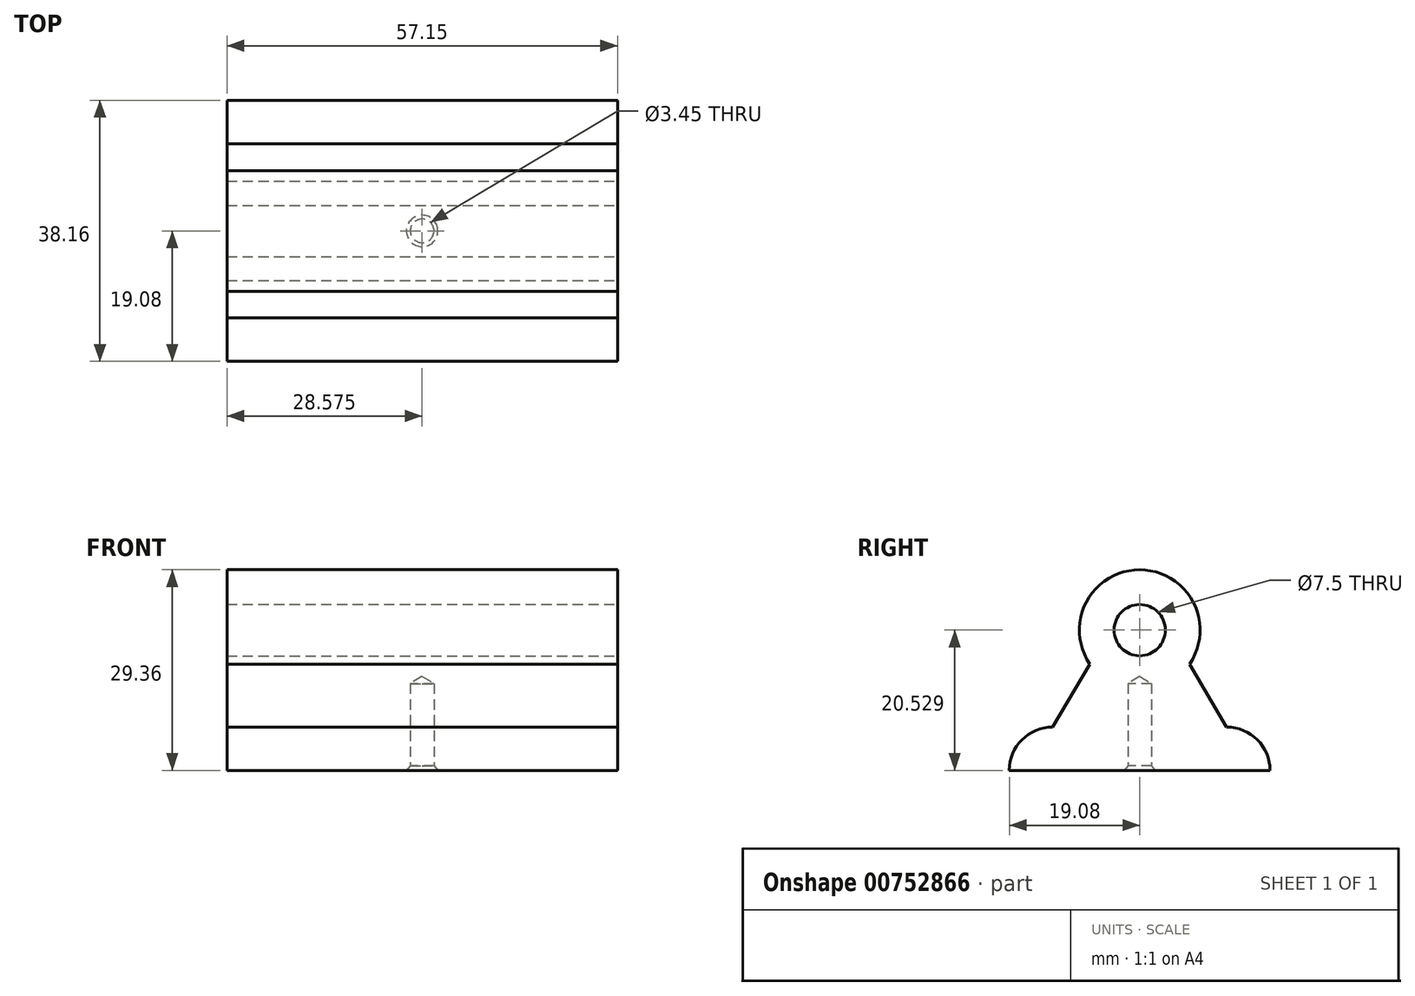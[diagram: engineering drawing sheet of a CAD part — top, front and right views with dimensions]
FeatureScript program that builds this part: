
annotation { "Feature Type Name" : "Feature", "Feature Type Description" : "" }
export const myFeature = defineFeature(function(context is Context, id is Id, definition is map)
    precondition{}
    {
        {
            var Q0;
            Q0=qCreatedBy(makeId("Right.planeOp"),FACE);
            var sketch = newSketch(context, id + "F0", { "sketchPlane" : qUnion([Q0])});
            skCircle(sketch, "E0", {"center": v(0, 2.7) * mm, "radius": 25 * mm});
            skCircle(sketch, "E1", {"center": v(0, 16.7) * mm, "radius": 11 * mm});
            skCircle(sketch, "E2", {"center": v(0, 16.7) * mm, "radius": 3.75 * mm});
            skLineSegment(sketch, "E3.bottom", {"start": v(12.73, 2.53) * mm, "end": v(-12.73, 2.53) * mm});
            skLineSegment(sketch, "E3.top", {"start": v(12.73, -10.17) * mm, "end": v(-12.73, -10.17) * mm});
            skLineSegment(sketch, "E3.left", {"start": v(19.08, -3.82) * mm, "end": v(19.08, -3.82) * mm});
            skLineSegment(sketch, "E3.right", {"start": v(-19.08, -3.82) * mm, "end": v(-19.08, -3.82) * mm});
            skPoint(sketch, "E3.middle", {"position": v(0, -3.82) * mm});
            skLineSegment(sketch, "E4", {"start": v(-19.08, -3.82) * mm, "end": v(19.08, -3.82) * mm});
            skPoint(sketch, "E5.visualSharp", {"position": v(-19.08, -10.17) * mm});
            skArc(sketch, "E5.filletArc", {"start": v(-19.08, -3.82) * mm, "mid": v(-17.22, -8.3) * mm, "end": v(-12.73, -10.17) * mm});
            skPoint(sketch, "E6.visualSharp", {"position": v(-19.08, 2.53) * mm});
            skArc(sketch, "E6.filletArc", {"start": v(-12.73, 2.53) * mm, "mid": v(-17.22, 0.67) * mm, "end": v(-19.08, -3.82) * mm});
            skPoint(sketch, "E7.visualSharp", {"position": v(19.08, 2.53) * mm});
            skArc(sketch, "E7.filletArc", {"start": v(19.08, -3.82) * mm, "mid": v(17.22, 0.67) * mm, "end": v(12.73, 2.53) * mm});
            skPoint(sketch, "E8.visualSharp", {"position": v(19.08, -10.17) * mm});
            skArc(sketch, "E8.filletArc", {"start": v(12.73, -10.17) * mm, "mid": v(17.22, -8.3) * mm, "end": v(19.08, -3.82) * mm});
            skLineSegment(sketch, "E9", {"start": v(-12.73, 2.53) * mm, "end": v(-3.23, 18.62) * mm});
            skLineSegment(sketch, "E10", {"start": v(12.73, 2.53) * mm, "end": v(3.23, 18.62) * mm});
            skLineSegment(sketch, "E11", {"start": v(0, 2.53) * mm, "end": v(0, -3.82) * mm});
            skLineSegment(sketch, "E12.bottom", {"start": v(-8.5, 2.53) * mm, "end": v(8.5, 2.53) * mm});
            skLineSegment(sketch, "E12.top", {"start": v(-8.5, -3.82) * mm, "end": v(8.5, -3.82) * mm});
            skLineSegment(sketch, "E12.left", {"start": v(-8.5, 2.53) * mm, "end": v(-8.5, -3.82) * mm});
            skLineSegment(sketch, "E12.right", {"start": v(8.5, 2.53) * mm, "end": v(8.5, -3.82) * mm});
            skPoint(sketch, "E12.middle", {"position": v(0, -0.64) * mm});
            skCircle(sketch, "E13", {"center": v(0, 16.7) * mm, "radius": 8.83 * mm});
            skSolve(sketch);
        }
        {
            var Q0;
            {var subQ0=sQuery(id+"F0.wireOp",EDGE,"E6.filletArc");Q0=makeQuery(id+"F0.imprint","IMPRINT",FACE,{"disambiguationData":[TD([[makeQuery(id+"F0.imprint","IMPRINT",EDGE,{"derivedFrom":subQ0}),1.0]])]});}
            var Q1;
            {var subQ0=sQuery(id+"F0.wireOp",EDGE,"E11");Q1=makeQuery(id+"F0.imprint","IMPRINT",FACE,{"disambiguationData":[TD([[makeQuery(id+"F0.imprint","IMPRINT",EDGE,{"derivedFrom":subQ0}),-1.0]])]});}
            var Q2;
            {var subQ0=sQuery(id+"F0.wireOp",EDGE,"E11");Q2=makeQuery(id+"F0.imprint","IMPRINT",FACE,{"disambiguationData":[TD([[makeQuery(id+"F0.imprint","IMPRINT",EDGE,{"derivedFrom":subQ0}),1.0]])]});}
            var Q3;
            {var subQ0=sQuery(id+"F0.wireOp",EDGE,"E7.filletArc");Q3=makeQuery(id+"F0.imprint","IMPRINT",FACE,{"disambiguationData":[TD([[makeQuery(id+"F0.imprint","IMPRINT",EDGE,{"derivedFrom":subQ0}),1.0]])]});}
            var Q4;
            {var subQ0=sQuery(id+"F0.wireOp",EDGE,"E9");var subQ3=sQuery(id+"F0.wireOp",EDGE,"E1");var subQ4=makeQuery(id+"F0.imprint","INTERSECT",VERTEX,{"derivedFrom":[subQ3,subQ0]});Q4=makeQuery(id+"F0.imprint","IMPRINT",FACE,{"disambiguationData":[TD([[makeQuery(id+"F0.imprint","IMPRINT",EDGE,{"disambiguationData":[TD([[subQ4,-1.0]])],"derivedFrom":subQ3}),-1.0]])]});}
            var Q5;
            {var subQ0=sQuery(id+"F0.wireOp",EDGE,"E9");var subQ1=sQuery(id+"F0.wireOp",EDGE,"E1");var subQ2=makeQuery(id+"F0.imprint","INTERSECT",VERTEX,{"derivedFrom":[subQ1,subQ0]});Q5=makeQuery(id+"F0.imprint","IMPRINT",FACE,{"disambiguationData":[TD([[makeQuery(id+"F0.imprint","IMPRINT",EDGE,{"disambiguationData":[TD([[subQ2,-1.0]])],"derivedFrom":subQ1}),1.0]])]});}
            var Q6;
            {var subQ0=sQuery(id+"F0.wireOp",EDGE,"E9");var subQ1=sQuery(id+"F0.wireOp",EDGE,"E2");var subQ2=makeQuery(id+"F0.imprint","INTERSECT",VERTEX,{"derivedFrom":[subQ1,subQ0]});Q6=makeQuery(id+"F0.imprint","IMPRINT",FACE,{"disambiguationData":[TD([[makeQuery(id+"F0.imprint","IMPRINT",EDGE,{"disambiguationData":[TD([[subQ2,1.0]])],"derivedFrom":subQ1}),-1.0]])]});}
            var Q7;
            {var subQ0=sQuery(id+"F0.wireOp",EDGE,"E9");var subQ1=sQuery(id+"F0.wireOp",EDGE,"E2");var subQ2=makeQuery(id+"F0.imprint","INTERSECT",VERTEX,{"derivedFrom":[subQ1,subQ0]});Q7=makeQuery(id+"F0.imprint","IMPRINT",FACE,{"disambiguationData":[TD([[makeQuery(id+"F0.imprint","IMPRINT",EDGE,{"disambiguationData":[TD([[subQ2,-1.0]])],"derivedFrom":subQ1}),-1.0]])]});}
            extrude(context, id + "F1", {"entities" : qUnion([Q0, Q1, Q2, Q3, Q4, Q5, Q6, Q7]), "depth" : -57.15 * mm, "offsetDistance" : 25.4 * mm});
        }
        {
            var Q0;
            Q0=makeQuery(id+"F1.opExtrude","SWEPT_FACE",FACE,{"disambiguationData":[OSD([sQuery(id+"F0.wireOp",EDGE,"E4"),sQuery(id+"F0.wireOp",EDGE,"E12.top")])]});
            var sketch = newSketch(context, id + "F2", { "sketchPlane" : qUnion([Q0])});
            skPoint(sketch, "E14", {"position": v(-28.58, 0) * mm});
            skPoint(sketch, "E14.positionSnap0", {"position": v(-28.58, -19.08) * mm});
            skLineSegment(sketch, "E15.bottom", {"start": v(-22.33, 0) * mm, "end": v(-34.82, 0) * mm});
            skLineSegment(sketch, "E15.top", {"start": v(-22.33, 0) * mm, "end": v(-34.82, 0) * mm});
            skLineSegment(sketch, "E15.left", {"start": v(-22.33, 0) * mm, "end": v(-22.33, 0) * mm});
            skLineSegment(sketch, "E15.right", {"start": v(-34.82, 0) * mm, "end": v(-34.82, 0) * mm});
            skSolve(sketch);
        }
        {
            var Q0;
            Q0=sQuery(id+"F2.wireOp",VERTEX,"E14");
            var Q1;
            Q1=makeQuery(id+"F1.opExtrude","SWEPT_BODY",BODY,{"disambiguationData":[OSD([sQuery(id+"F0.wireOp",EDGE,"E2"),sQuery(id+"F0.wireOp",EDGE,"E4"),sQuery(id+"F0.wireOp",EDGE,"E6.filletArc"),sQuery(id+"F0.wireOp",EDGE,"E7.filletArc"),sQuery(id+"F0.wireOp",EDGE,"E9"),sQuery(id+"F0.wireOp",EDGE,"E10"),sQuery(id+"F0.wireOp",EDGE,"E12.top"),sQuery(id+"F0.wireOp",EDGE,"E13")])]});
            hole(context, id + "F3", {"style" : HoleStyle.C_SINK, "endStyle" : HoleEndStyle.BLIND, "holeDiameter" : 3.45 * mm, "cSinkDiameter" : 4.6 * mm, "cSinkAngle" : 82 * degree, "majorDiameter" : 6.35 * mm, "holeDepth" : 12.7 * mm, "isTappedThrough" : true, "tappedDepth" : 12.7 * mm, "tapClearance" : 3, "locations" : qUnion([Q0]), "scope" : qUnion([Q1])});
        }
    });
